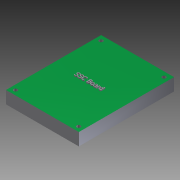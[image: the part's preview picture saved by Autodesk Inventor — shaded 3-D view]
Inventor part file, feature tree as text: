
AUTODESK INVENTOR PART (.ipt)
format: ipt  version: 2012 (Build 160160000, 160)  size: 387,584 bytes
history: native  units: mm
features: sketch x2, extrude x1, hole x1, emboss x1
ambient origin geometry x8: Origin, YZ Plane, XZ Plane, XY Plane, X Axis, Y Axis, Z Axis, Center Point
bodies: Solid1 (feature_tree)
feature tree (5):
  extrude  "Extrusion1"  Depth=10.0mm TaperAngle=0.0deg
  sketch  "Sketch2"  dims[d11=3.0mm d12=3.0mm d13=3.0mm d14=58.44mm d15=76.3mm d16=50.55mm d17=68.5mm d18=68.5mm d19=50.55mm d20=3.0mm d21=6.0mm d22=4.0mm d23=2.0mm d24=90.0deg d25=8.0mm d26=20.594885mm d27=1.0mm d28=0.0mm]
  hole  "Hole1"  [1 undecoded]
  emboss  "Emboss1"
  sketch  "Sketch1"  dims[d0=3.0mm d1=3.0mm d2=3.0mm d3=58.44mm d4=76.3mm d5=50.55mm d6=68.5mm d7=68.5mm d8=50.55mm d9=10.0mm d10=0.0mm]
note: 1 required parameter value undecoded (feature->parameter linkage not recoverable at this tier; creation-order binding heuristic only, values carry confidence <= 0.55)
